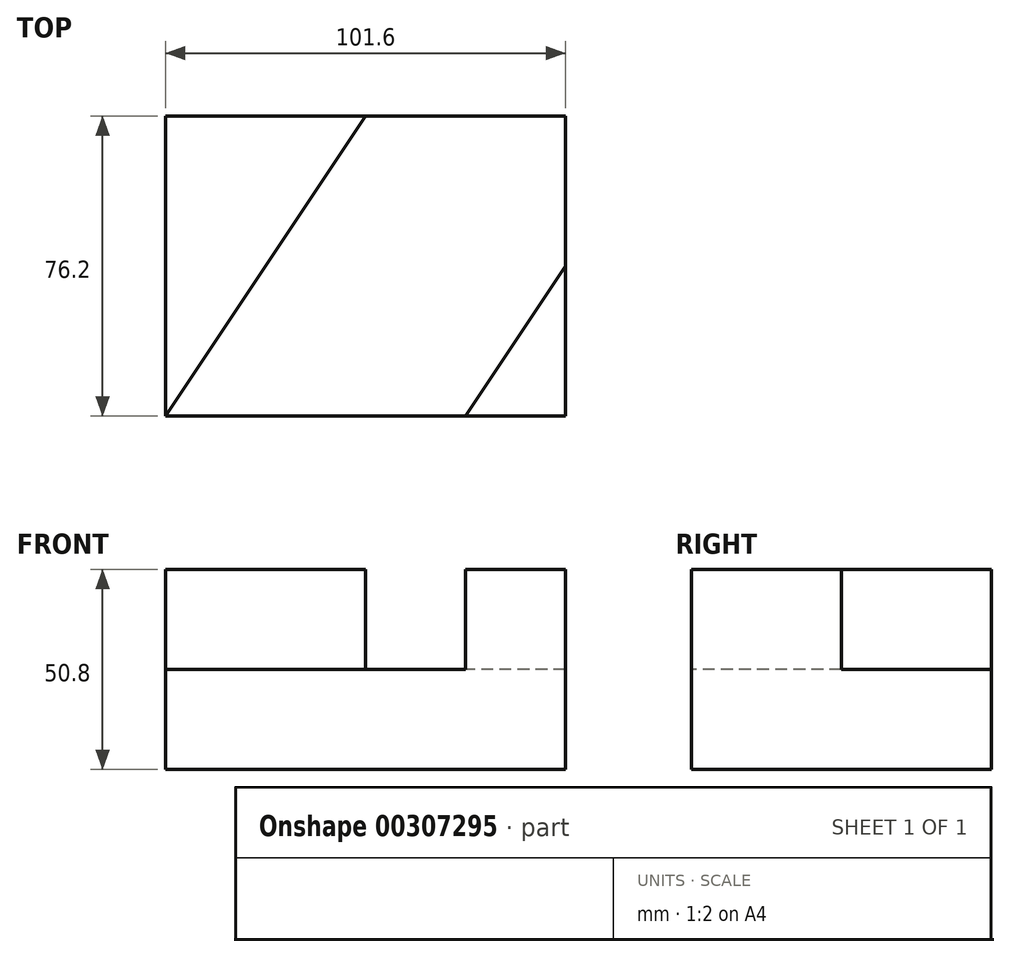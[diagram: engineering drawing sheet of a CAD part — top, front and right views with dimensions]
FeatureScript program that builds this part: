
annotation { "Feature Type Name" : "Feature", "Feature Type Description" : "" }
export const myFeature = defineFeature(function(context is Context, id is Id, definition is map)
    precondition{}
    {
        {
            var Q0;
            Q0=qCreatedBy(makeId("Top.planeOp"),FACE);
            var sketch = newSketch(context, id + "F0", { "sketchPlane" : qUnion([Q0])});
            skLineSegment(sketch, "E0", {"start": v(-63.15, -68.75) * mm, "end": v(38.45, -68.75) * mm});
            skLineSegment(sketch, "E1", {"start": v(38.45, -68.75) * mm, "end": v(38.45, 7.45) * mm});
            skLineSegment(sketch, "E2", {"start": v(38.45, 7.45) * mm, "end": v(-63.15, 7.45) * mm});
            skLineSegment(sketch, "E3", {"start": v(-63.15, 7.45) * mm, "end": v(-63.15, -68.75) * mm});
            skSolve(sketch);
        }
        {
            var Q0;
            Q0=makeQuery(id+"F0.imprint","IMPRINT",FACE,{"disambiguationData":[TD([[makeQuery(id+"F0.imprint","IMPRINT",EDGE,{"derivedFrom":sQuery(id+"F0.wireOp",EDGE,"E0")}),1.0]])]});
            extrude(context, id + "F1", {"entities" : qUnion([Q0]), "depth" : 25.4 * mm});
        }
        {
            var Q0;
            Q0=makeQuery(id+"F1.opExtrude","CAP_FACE",FACE,{"disambiguationData":[OSD([sQuery(id+"F0.wireOp",EDGE,"E0"),sQuery(id+"F0.wireOp",EDGE,"E1"),sQuery(id+"F0.wireOp",EDGE,"E2"),sQuery(id+"F0.wireOp",EDGE,"E3")])],"isStart":false});
            var sketch = newSketch(context, id + "F2", { "sketchPlane" : qUnion([Q0])});
            skLineSegment(sketch, "E4", {"start": v(-12.35, 7.45) * mm, "end": v(-63.15, 7.45) * mm});
            skLineSegment(sketch, "E5", {"start": v(-63.15, 7.45) * mm, "end": v(-63.15, -68.75) * mm});
            skLineSegment(sketch, "E6", {"start": v(-12.35, 7.45) * mm, "end": v(-63.15, -68.75) * mm});
            skLineSegment(sketch, "E7", {"start": v(13.05, -68.75) * mm, "end": v(38.45, -68.75) * mm});
            skLineSegment(sketch, "E8", {"start": v(38.45, -68.75) * mm, "end": v(38.45, -30.65) * mm});
            skLineSegment(sketch, "E9", {"start": v(38.45, -30.65) * mm, "end": v(13.05, -68.75) * mm});
            skSolve(sketch);
        }
        {
            var Q0;
            Q0=makeQuery(id+"F2.imprint","IMPRINT",FACE,{"disambiguationData":[TD([[makeQuery(id+"F2.imprint","IMPRINT",EDGE,{"derivedFrom":sQuery(id+"F2.wireOp",EDGE,"E4")}),1.0]])]});
            extrude(context, id + "F3", {"entities" : qUnion([Q0]), "operationType" : NewBodyOperationType.ADD, "depth" : 25.4 * mm});
        }
        {
            var Q0;
            Q0=makeQuery(id+"F1.opExtrude","CAP_FACE",FACE,{"disambiguationData":[OSD([sQuery(id+"F0.wireOp",EDGE,"E0"),sQuery(id+"F0.wireOp",EDGE,"E1"),sQuery(id+"F0.wireOp",EDGE,"E2"),sQuery(id+"F0.wireOp",EDGE,"E3")])],"isStart":false});
            var sketch = newSketch(context, id + "F4", { "sketchPlane" : qUnion([Q0])});
            skLineSegment(sketch, "E10", {"start": v(13.05, -68.75) * mm, "end": v(38.45, -68.75) * mm});
            skLineSegment(sketch, "E11", {"start": v(38.45, -68.75) * mm, "end": v(38.45, -30.65) * mm});
            skLineSegment(sketch, "E12", {"start": v(38.45, -30.65) * mm, "end": v(13.05, -68.75) * mm});
            skSolve(sketch);
        }
        {
            var Q0;
            Q0=makeQuery(id+"F4.imprint","IMPRINT",FACE,{"disambiguationData":[TD([[makeQuery(id+"F4.imprint","IMPRINT",EDGE,{"derivedFrom":sQuery(id+"F4.wireOp",EDGE,"E10")}),1.0]])]});
            extrude(context, id + "F5", {"entities" : qUnion([Q0]), "operationType" : NewBodyOperationType.ADD, "depth" : 25.4 * mm});
        }
    });
